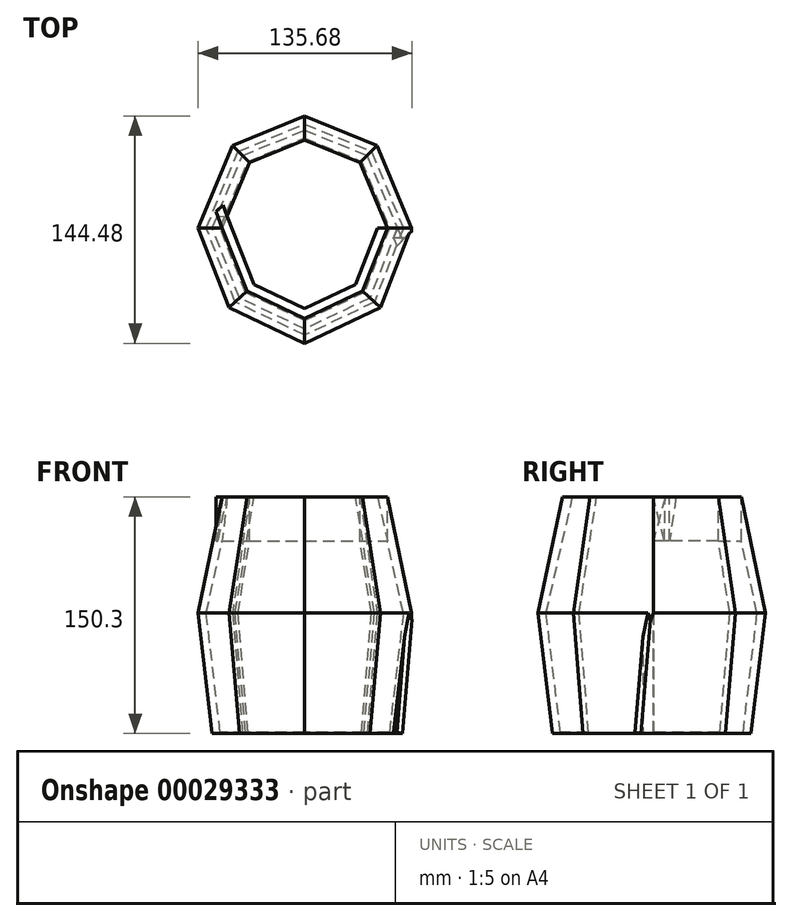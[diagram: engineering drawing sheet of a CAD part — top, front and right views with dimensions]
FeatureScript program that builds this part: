
annotation { "Feature Type Name" : "Feature", "Feature Type Description" : "" }
export const myFeature = defineFeature(function(context is Context, id is Id, definition is map)
    precondition{}
    {
        {
            var Q0;
            Q0=qCreatedBy(makeId("Front.planeOp"),FACE);
            var sketch = newSketch(context, id + "F0", { "sketchPlane" : qUnion([Q0])});
            skLineSegment(sketch, "E0", {"start": v(52.4, 73.83) * mm, "end": v(77.11, 0) * mm});
            skLineSegment(sketch, "E1", {"start": v(77.11, 0) * mm, "end": v(72.87, -75.76) * mm});
            skLineSegment(sketch, "E2", {"start": v(72.87, -75.76) * mm, "end": v(70.57, -75.63) * mm});
            skLineSegment(sketch, "E3", {"start": v(70.57, -75.63) * mm, "end": v(70.57, 0) * mm});
            skLineSegment(sketch, "E4", {"start": v(70.57, 0) * mm, "end": v(46.23, 73.83) * mm});
            skLineSegment(sketch, "E5", {"start": v(46.23, 73.83) * mm, "end": v(52.4, 73.83) * mm});
            skLineSegment(sketch, "E6", {"start": v(52.4, 73.83) * mm, "end": v(52.4, 76.2) * mm});
            skLineSegment(sketch, "E7", {"start": v(52.4, 76.2) * mm, "end": v(46.23, 76.2) * mm});
            skLineSegment(sketch, "E8", {"start": v(46.23, 76.2) * mm, "end": v(46.23, 73.83) * mm});
            skSolve(sketch);
        }
        {
            var Q0;
            Q0=makeQuery(id+"F0.imprint","IMPRINT",FACE,{"disambiguationData":[TD([[makeQuery(id+"F0.imprint","IMPRINT",EDGE,{"derivedFrom":sQuery(id+"F0.wireOp",EDGE,"E5")}),1.0]])]});
            extrude(context, id + "F1", {"entities" : qUnion([Q0]), "depth" : 25.4 * mm});
        }
        {
            var Q0;
            Q0=makeQuery(id+"F1.opExtrude","CAP_FACE",FACE,{"disambiguationData":[OSD([sQuery(id+"F0.wireOp",EDGE,"E5"),sQuery(id+"F0.wireOp",EDGE,"E6"),sQuery(id+"F0.wireOp",EDGE,"E7"),sQuery(id+"F0.wireOp",EDGE,"E8")])],"isStart":true});
            var sketch = newSketch(context, id + "F2", { "sketchPlane" : qUnion([Q0])});
            skLineSegment(sketch, "E9", {"start": v(-46.23, 73.83) * mm, "end": v(-62.55, 0) * mm});
            skLineSegment(sketch, "E10", {"start": v(-62.55, 0) * mm, "end": v(-53.67, -75.88) * mm});
            skLineSegment(sketch, "E11", {"start": v(-53.67, -75.88) * mm, "end": v(-58.74, -76.47) * mm});
            skLineSegment(sketch, "E12", {"start": v(-58.74, -76.47) * mm, "end": v(-67.69, 0) * mm});
            skLineSegment(sketch, "E13", {"start": v(-67.69, 0) * mm, "end": v(-52.4, 73.83) * mm});
            skLineSegment(sketch, "E14", {"start": v(-52.4, 73.83) * mm, "end": v(-46.23, 73.83) * mm});
            skSolve(sketch);
        }
        {
            var Q0;
            Q0=makeQuery(id+"F1.opExtrude","SWEPT_FACE",FACE,{"disambiguationData":[OSD([sQuery(id+"F0.wireOp",EDGE,"E8")])]});
            extrude(context, id + "F3", {"entities" : qUnion([Q0]), "operationType" : NewBodyOperationType.ADD, "depth" : 59.6 * mm});
        }
        {
            var Q0;
            Q0=qCreatedBy(makeId("Front.planeOp"),FACE);
            var sketch = newSketch(context, id + "F4", { "sketchPlane" : qUnion([Q0])});
            skLineSegment(sketch, "E15", {"start": v(0, 0) * mm, "end": v(67.7, 0) * mm});
            skLineSegment(sketch, "E16", {"start": v(67.7, 0) * mm, "end": v(51.46, -5.84) * mm});
            skLineSegment(sketch, "E17", {"start": v(51.46, -5.84) * mm, "end": v(0, 0) * mm});
            skSolve(sketch);
        }
        {
            var Q0;
            Q0=makeQuery(id+"F4.imprint","IMPRINT",FACE,{"disambiguationData":[TD([[makeQuery(id+"F4.imprint","IMPRINT",EDGE,{"derivedFrom":sQuery(id+"F4.wireOp",EDGE,"E15")}),-1.0]])]});
            extrude(context, id + "F5", {"entities" : qUnion([Q0]), "oppositeDirection" : true, "depth" : 36.27 * mm});
        }
        {
            var Q0;
            Q0=makeQuery(id+"F5.opExtrude","SWEPT_FACE",FACE,{"disambiguationData":[OSD([sQuery(id+"F4.wireOp",EDGE,"E15")])]});
            var sketch = newSketch(context, id + "F6", { "sketchPlane" : qUnion([Q0])});
            skLineSegment(sketch, "E18", {"start": v(0, 0) * mm, "end": v(0, -90.12) * mm});
            skLineSegment(sketch, "E19", {"start": v(0, -90.12) * mm, "end": v(43.26, -62.74) * mm});
            skLineSegment(sketch, "E20", {"start": v(43.26, -62.74) * mm, "end": v(67.7, 0) * mm});
            skLineSegment(sketch, "E21", {"start": v(0, -73.31) * mm, "end": v(48, -50.58) * mm});
            skLineSegment(sketch, "E22", {"start": v(48, -50.58) * mm, "end": v(67.7, 0) * mm});
            skLineSegment(sketch, "E23.MirrorCS", {"start": v(-48, -50.58) * mm, "end": v(-67.7, 0) * mm});
            skLineSegment(sketch, "E24.MirrorCS", {"start": v(0, -73.31) * mm, "end": v(-48, -50.58) * mm});
            skSolve(sketch);
        }
        {
            var Q0;
            Q0=makeQuery(id+"F2.imprint","IMPRINT",FACE,{"disambiguationData":[TD([[makeQuery(id+"F2.imprint","IMPRINT",EDGE,{"derivedFrom":sQuery(id+"F2.wireOp",EDGE,"E9")}),-1.0]])]});
            var Q1;
            Q1=sQuery(id+"F6.wireOp",EDGE,"E22");
            var Q2;
            Q2=sQuery(id+"F6.wireOp",EDGE,"E21");
            var Q3;
            Q3=sQuery(id+"F6.wireOp",EDGE,"E24.MirrorCS");
            var Q4;
            Q4=sQuery(id+"F6.wireOp",EDGE,"E23.MirrorCS");
            sweep(context, id + "F7", {"profiles" : qUnion([Q0]), "path" : qUnion([Q1, Q2, Q3, Q4])});
        }
        {
            var Q0;
            Q0=makeQuery(id+"F1.opExtrude","SWEPT_BODY",BODY,{"disambiguationData":[OSD([sQuery(id+"F0.wireOp",EDGE,"E5"),sQuery(id+"F0.wireOp",EDGE,"E6"),sQuery(id+"F0.wireOp",EDGE,"E7"),sQuery(id+"F0.wireOp",EDGE,"E8")])]});
            deleteBodies(context, id + "F8", {"entities" : qUnion([Q0])});
        }
        {
            var Q0;
            Q0=makeQuery(id+"F7.opSweep","SWEPT_FACE",FACE,{"disambiguationData":[OSD([sQuery(id+"F2.wireOp",EDGE,"E14"),sQuery(id+"F6.wireOp",EDGE,"E22")])]});
            var sketch = newSketch(context, id + "F9", { "sketchPlane" : qUnion([Q0])});
            skLineSegment(sketch, "E25", {"start": v(52.4, 0) * mm, "end": v(-52.4, 0) * mm});
            skLineSegment(sketch, "E26", {"start": v(-51.88, 14.52) * mm, "end": v(-32.24, -35.91) * mm});
            skLineSegment(sketch, "E27", {"start": v(-52.4, 0) * mm, "end": v(-79.96, 0) * mm});
            skLineSegment(sketch, "E28", {"start": v(-79.96, 0) * mm, "end": v(-79.96, 37.9) * mm});
            skLineSegment(sketch, "E29", {"start": v(-79.96, 37.9) * mm, "end": v(-51.88, 14.52) * mm});
            skSolve(sketch);
        }
        {
            var Q0;
            {var subQ2=sQuery(id+"F9.wireOp",EDGE,"E27");Q0=makeQuery(id+"F9.imprint","IMPRINT",FACE,{"disambiguationData":[TD([[makeQuery(id+"F9.imprint","IMPRINT",EDGE,{"derivedFrom":subQ2}),-1.0]])]});}
            var Q1;
            {var subQ0=sQuery(id+"F2.wireOp",EDGE,"E14");var subQ4=makeQuery(id+"F7.opSweep","CAP_EDGE",EDGE,{"disambiguationData":[OSD([subQ0,sQuery(id+"F6.wireOp",VERTEX,"E23.MirrorCS.end")])],"isStart":false});Q1=makeQuery(id+"F9.imprint","IMPRINT",FACE,{"disambiguationData":[TD([[makeQuery(id+"F9.imprint","IMPRINT",EDGE,{"derivedFrom":subQ4}),1.0]])]});}
            extrude(context, id + "F10", {"entities" : qUnion([Q0, Q1]), "operationType" : NewBodyOperationType.REMOVE, "oppositeDirection" : true, "depth" : 158.35 * mm});
        }
        {
            var Q0;
            Q0=makeQuery(id+"F5.opExtrude","SWEPT_BODY",BODY,{"disambiguationData":[OSD([sQuery(id+"F4.wireOp",EDGE,"E15"),sQuery(id+"F4.wireOp",EDGE,"E16"),sQuery(id+"F4.wireOp",EDGE,"E17")])]});
            deleteBodies(context, id + "F11", {"entities" : qUnion([Q0])});
        }
        {
            var Q0;
            Q0=qCreatedBy(makeId("Top.planeOp"),FACE);
            var sketch = newSketch(context, id + "F12", { "sketchPlane" : qUnion([Q0])});
            skLineSegment(sketch, "E30", {"start": v(0, 0) * mm, "end": v(0, 73.25) * mm});
            skLineSegment(sketch, "E31", {"start": v(0, 73.25) * mm, "end": v(47.39, 53.76) * mm});
            skLineSegment(sketch, "E32", {"start": v(47.39, 53.76) * mm, "end": v(69.78, 0) * mm});
            skLineSegment(sketch, "E33.MirrorCS", {"start": v(0, 73.25) * mm, "end": v(-47.39, 53.76) * mm});
            skLineSegment(sketch, "E34.MirrorCS", {"start": v(-47.39, 53.76) * mm, "end": v(-69.78, 0) * mm});
            skSolve(sketch);
        }
        {
            var Q0;
            Q0=makeQuery(id+"F10.boolean.opBoolean","COPY",FACE,{"derivedFrom":makeQuery(id+"F10.opExtrude","SWEPT_FACE",FACE,{"disambiguationData":[OSD([sQuery(id+"F9.wireOp",EDGE,"E25"),sQuery(id+"F9.wireOp",EDGE,"E27")])]})});
            var Q1;
            Q1=sQuery(id+"F12.wireOp",EDGE,"E34.MirrorCS");
            var Q2;
            Q2=sQuery(id+"F12.wireOp",EDGE,"E33.MirrorCS");
            var Q3;
            Q3=sQuery(id+"F12.wireOp",EDGE,"E31");
            var Q4;
            Q4=sQuery(id+"F12.wireOp",EDGE,"E32");
            sweep(context, id + "F13", {"operationType" : NewBodyOperationType.ADD, "profiles" : qUnion([Q0]), "path" : qUnion([Q1, Q2, Q3, Q4])});
        }
        {
            var Q0;
            Q0=makeQuery(id+"F7.opSweep","SWEPT_FACE",FACE,{"disambiguationData":[OSD([sQuery(id+"F2.wireOp",EDGE,"E13"),sQuery(id+"F6.wireOp",EDGE,"E22")])]});
            var sketch = newSketch(context, id + "F14", { "sketchPlane" : qUnion([Q0])});
            skLineSegment(sketch, "E35", {"start": v(0, -11.98) * mm, "end": v(0, 63.42) * mm});
            skSolve(sketch);
        }
        {
            var Q0;
            {var subQ3=sQuery(id+"F14.wireOp",EDGE,"E35");Q0=makeQuery(id+"F14.imprint","IMPRINT",FACE,{"disambiguationData":[TD([[makeQuery(id+"F14.imprint","IMPRINT",EDGE,{"derivedFrom":subQ3}),1.0]])]});}
            extrude(context, id + "F15", {"entities" : qUnion([Q0]), "operationType" : NewBodyOperationType.ADD, "depth" : 25.4 * mm});
        }
        {
            var Q0;
            Q0=makeQuery(id+"F15.opExtrude","SWEPT_FACE",FACE,{"disambiguationData":[OSD([sQuery(id+"F14.wireOp",EDGE,"E35")])]});
            extrude(context, id + "F16", {"entities" : qUnion([Q0]), "operationType" : NewBodyOperationType.REMOVE, "depth" : 55.9 * mm});
        }
        {
            var Q0;
            Q0=makeQuery(id+"F15.opExtrude","SWEPT_FACE",FACE,{"disambiguationData":[OSD([sQuery(id+"F2.wireOp",EDGE,"E13"),sQuery(id+"F6.wireOp",VERTEX,"E21.end")])]});
            extrude(context, id + "F17", {"entities" : qUnion([Q0]), "operationType" : NewBodyOperationType.REMOVE, "oppositeDirection" : true, "depth" : 85.12 * mm});
        }
        {
            var Q0;
            Q0=makeQuery(id+"F15.opExtrude","SWEPT_FACE",FACE,{"disambiguationData":[OSD([sQuery(id+"F0.wireOp",EDGE,"E6"),sQuery(id+"F2.wireOp",EDGE,"E13"),sQuery(id+"F2.wireOp",EDGE,"E14"),sQuery(id+"F6.wireOp",EDGE,"E22")])]});
            extrude(context, id + "F18", {"entities" : qUnion([Q0]), "operationType" : NewBodyOperationType.REMOVE, "oppositeDirection" : true, "depth" : 25.4 * mm});
        }
        {
            var Q0;
            Q0=makeQuery(id+"F15.opExtrude","SWEPT_FACE",FACE,{"disambiguationData":[OSD([sQuery(id+"F14.wireOp",EDGE,"E35")])]});
            extrude(context, id + "F19", {"entities" : qUnion([Q0]), "operationType" : NewBodyOperationType.REMOVE, "oppositeDirection" : true, "depth" : 25.4 * mm});
        }
    });
